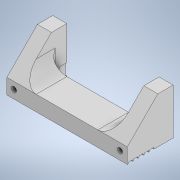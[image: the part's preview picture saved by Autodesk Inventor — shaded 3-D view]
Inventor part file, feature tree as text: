
AUTODESK INVENTOR PART (.ipt)
format: ipt  version: 2021 (Build 250183000, 183)  size: 562,176 bytes
history: native  units: in
note: dims shown in document units (in); Inventor stores cm internally (conversion verified against a paired STEP export)
features: sketch x8, extrude x7, projected_geometry x7, mirror x4, pattern_linear x3, fillet x2, chamfer x2, hole x1
ambient origin geometry x8: Origin, YZ Plane, XZ Plane, XY Plane, X Axis, Y Axis, Z Axis, Center Point
bodies: Solid1 (feature_tree)
feature tree (34):
  extrude  "Extrusion1"  Depth=0.5in
  extrude  "Extrusion2"  Depth=0.5in
  mirror  "Mirror1"
  fillet  "Fillet1"  Radius=0.5in
  extrude  "Extrusion3"  Depth=0.125in
  pattern_linear  "Rectangular Pattern1"  Count1=11 Spacing1=0.25in
  extrude  "Extrusion4"  Depth=0.375in
  mirror  "Mirror2"
  hole  "Hole1"  [1 undecoded]
  mirror  "Mirror3"
  extrude  "Extrusion5"  Depth=0.19in
  chamfer  "Chamfer2"  Distance=0.236in
  fillet  "Fillet3"  Radius=0.8108in
  chamfer  "Chamfer3"  Distance=1.0in
  extrude  "Extrusion9"  Depth=0.125in TaperAngle=45.0deg
  pattern_linear  "Rectangular Pattern5"  Spacing1=0.5in  [1 undecoded]
  extrude  "Extrusion10"  Depth=0.125in TaperAngle=45.0deg
  pattern_linear  "Rectangular Pattern6"  Spacing1=4.1in  [1 undecoded]
  mirror  "Mirror5"
  sketch  "Sketch1"  dims[d0=3.938in d1=0.5in]
  sketch  "Sketch2"  dims[d2=1.0in d3=0.0in d4=0.46in d5=0.5in d6=0.0in]
  projected_geometry  "Projected Loop1"
  sketch  "Sketch3"  dims[d7=0.125in d9=0.162in]
  projected_geometry  "Projected Loop2"
  sketch  "Sketch4"  dims[d10=0.087in]
  projected_geometry  "Projected Loop3"
  projected_geometry  "Projected Loop4"
  sketch  "Sketch5"  dims[d11=0.0625in d12=0.0in d13=4.3307in d15=0.25in]
  projected_geometry  "Projected Loop5"
  projected_geometry  "Projected Loop6"
  sketch  "Sketch6"  dims[d19=0.04in d20=0.375in]
  projected_geometry  "Projected Loop7"
  sketch  "Sketch9"  dims[d21=0.02in d22=0.25in d23=0.0in]
  sketch  "Sketch10"  dims[d24=0.266in d25=0.276in d26=0.236in d27=0.17in d28=0.75in d29=0.507in d30=0.25in d31=0.5635in d32=0.12in d33=0.8108in d34=1.0in d35=0.0in d36=1.0in d37=0.125in d38=45.0deg d39=0.5in d41=0.01in d42=0.125in d43=45.0deg d71=4.1in d72=0.15in d73=0.125in d74=2.05in d75=0.05in d76=-0.1031in d77=1.9685in d79=0.175in d80=0.125in d81=0.51in d82=0.05in d83=0.05in d84=0.0in d85=0.7874in d87=0.19in]
note: 3 required parameter values undecoded (feature->parameter linkage not recoverable at this tier; creation-order binding heuristic only, values carry confidence <= 0.55)
